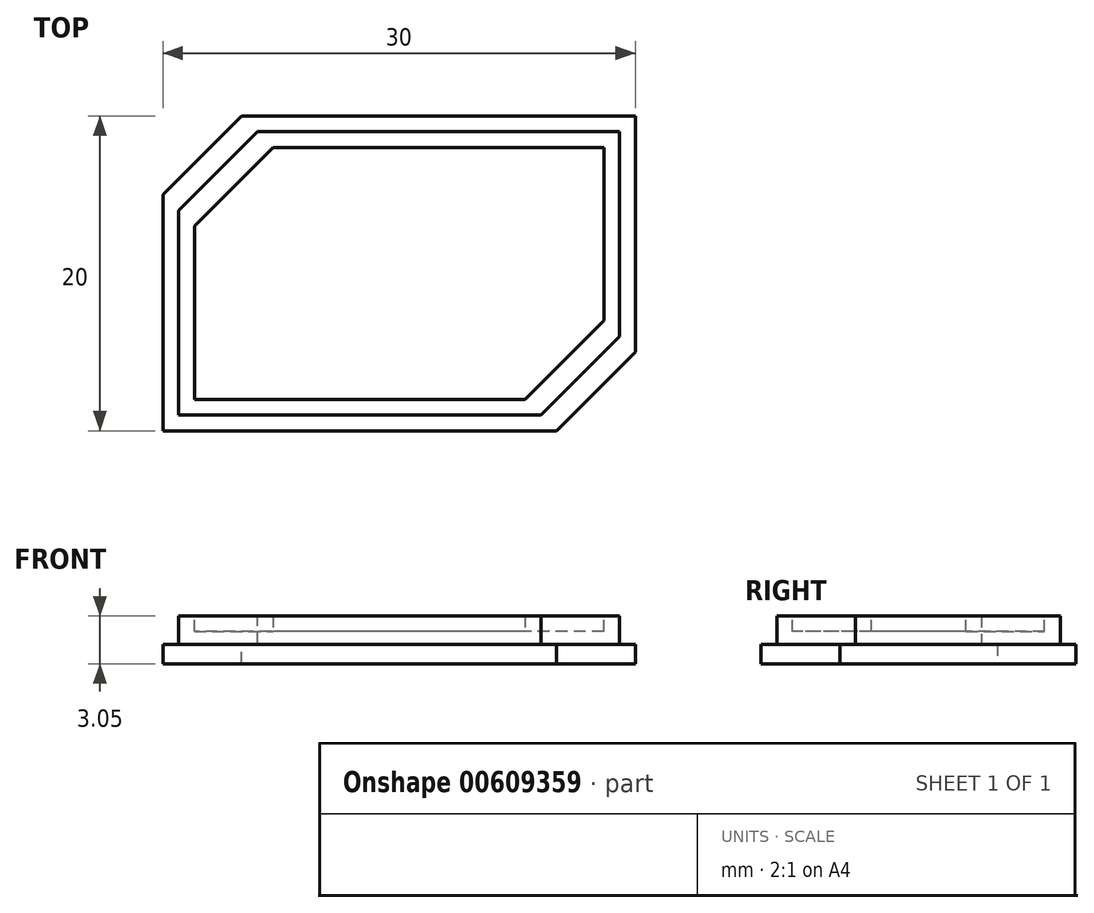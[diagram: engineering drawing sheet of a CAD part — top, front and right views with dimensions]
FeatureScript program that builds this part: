
annotation { "Feature Type Name" : "Feature", "Feature Type Description" : "" }
export const myFeature = defineFeature(function(context is Context, id is Id, definition is map)
    precondition{}
    {
        {
            var Q0;
            Q0=qCreatedBy(makeId("Top.planeOp"),FACE);
            var sketch = newSketch(context, id + "F0", { "sketchPlane" : qUnion([Q0])});
            skLineSegment(sketch, "E0.bottom", {"start": v(15, -10) * mm, "end": v(-15, -10) * mm});
            skLineSegment(sketch, "E0.top", {"start": v(15, 10) * mm, "end": v(-15, 10) * mm});
            skLineSegment(sketch, "E0.left", {"start": v(15, -10) * mm, "end": v(15, 10) * mm});
            skLineSegment(sketch, "E0.right", {"start": v(-15, -10) * mm, "end": v(-15, 10) * mm});
            skPoint(sketch, "E0.middle", {"position": v(0, 0) * mm});
            skSolve(sketch);
        }
        {
            var Q0;
            Q0=makeQuery(id+"F0.imprint","IMPRINT",FACE,{"disambiguationData":[TD([[makeQuery(id+"F0.imprint","IMPRINT",EDGE,{"derivedFrom":sQuery(id+"F0.wireOp",EDGE,"E0.bottom")}),-1.0]])]});
            extrude(context, id + "F1", {"entities" : qUnion([Q0]), "depth" : 1.25 * mm});
        }
        {
            var Q0;
            Q0=makeQuery(id+"F1.opExtrude","CAP_FACE",FACE,{"disambiguationData":[OSD([sQuery(id+"F0.wireOp",EDGE,"E0.bottom"),sQuery(id+"F0.wireOp",EDGE,"E0.top"),sQuery(id+"F0.wireOp",EDGE,"E0.left"),sQuery(id+"F0.wireOp",EDGE,"E0.right")])],"isStart":false});
            var sketch = newSketch(context, id + "F2", { "sketchPlane" : qUnion([Q0])});
            skLineSegment(sketch, "E1.bottom", {"start": v(14, -9) * mm, "end": v(-14, -9) * mm});
            skLineSegment(sketch, "E1.top", {"start": v(14, 9) * mm, "end": v(-14, 9) * mm});
            skLineSegment(sketch, "E1.left", {"start": v(14, -9) * mm, "end": v(14, 9) * mm});
            skLineSegment(sketch, "E1.right", {"start": v(-14, -9) * mm, "end": v(-14, 9) * mm});
            skPoint(sketch, "E1.middle", {"position": v(0, 0) * mm});
            skSolve(sketch);
        }
        {
            var Q0;
            Q0=makeQuery(id+"F2.imprint","IMPRINT",FACE,{"disambiguationData":[TD([[makeQuery(id+"F2.imprint","IMPRINT",EDGE,{"derivedFrom":sQuery(id+"F2.wireOp",EDGE,"E1.bottom")}),-1.0]])]});
            extrude(context, id + "F3", {"entities" : qUnion([Q0]), "operationType" : NewBodyOperationType.ADD, "depth" : 1.8 * mm, "offsetDistance" : 25 * mm});
        }
        {
            var Q0;
            Q0=makeQuery(id+"F3.opExtrude","CAP_FACE",FACE,{"disambiguationData":[OSD([sQuery(id+"F2.wireOp",EDGE,"E1.bottom"),sQuery(id+"F2.wireOp",EDGE,"E1.top"),sQuery(id+"F2.wireOp",EDGE,"E1.left"),sQuery(id+"F2.wireOp",EDGE,"E1.right")])],"isStart":false});
            var sketch = newSketch(context, id + "F4", { "sketchPlane" : qUnion([Q0])});
            skLineSegment(sketch, "E2.bottom", {"start": v(13, 8) * mm, "end": v(-13, 8) * mm});
            skLineSegment(sketch, "E2.top", {"start": v(13, -8) * mm, "end": v(-13, -8) * mm});
            skLineSegment(sketch, "E2.left", {"start": v(13, 8) * mm, "end": v(13, -8) * mm});
            skLineSegment(sketch, "E2.right", {"start": v(-13, 8) * mm, "end": v(-13, -8) * mm});
            skPoint(sketch, "E2.middle", {"position": v(0, 0) * mm});
            skSolve(sketch);
        }
        {
            var Q0;
            Q0=makeQuery(id+"F4.imprint","IMPRINT",FACE,{"disambiguationData":[TD([[makeQuery(id+"F4.imprint","IMPRINT",EDGE,{"derivedFrom":sQuery(id+"F4.wireOp",EDGE,"E2.bottom")}),1.0]])]});
            extrude(context, id + "F5", {"entities" : qUnion([Q0]), "operationType" : NewBodyOperationType.REMOVE, "oppositeDirection" : true, "depth" : 1 * mm, "offsetDistance" : 25 * mm});
        }
        {
            var Q0;
            Q0=makeQuery(id+"F5.boolean.opBoolean","COPY",EDGE,{"derivedFrom":makeQuery(id+"F5.opExtrude","SWEPT_EDGE",EDGE,{"disambiguationData":[OSD([sQuery(id+"F4.wireOp",EDGE,"E2.bottom"),sQuery(id+"F4.wireOp",EDGE,"E2.right")])]})});
            var Q1;
            Q1=makeQuery(id+"F5.boolean.opBoolean","COPY",EDGE,{"derivedFrom":makeQuery(id+"F5.opExtrude","SWEPT_EDGE",EDGE,{"disambiguationData":[OSD([sQuery(id+"F4.wireOp",EDGE,"E2.top"),sQuery(id+"F4.wireOp",EDGE,"E2.left")])]})});
            var Q2;
            Q2=makeQuery(id+"F3.opExtrude","SWEPT_EDGE",EDGE,{"disambiguationData":[OSD([sQuery(id+"F2.wireOp",EDGE,"E1.top"),sQuery(id+"F2.wireOp",EDGE,"E1.right")])]});
            var Q3;
            Q3=makeQuery(id+"F3.opExtrude","SWEPT_EDGE",EDGE,{"disambiguationData":[OSD([sQuery(id+"F2.wireOp",EDGE,"E1.bottom"),sQuery(id+"F2.wireOp",EDGE,"E1.left")])]});
            chamfer(context, id + "F6", {"entities" : qUnion([Q0, Q1, Q2, Q3]), "width" : 5 * mm, "tangentPropagation" : true});
        }
        {
            var Q0;
            Q0=makeQuery(id+"F1.opExtrude","SWEPT_EDGE",EDGE,{"disambiguationData":[OSD([sQuery(id+"F0.wireOp",EDGE,"E0.bottom"),sQuery(id+"F0.wireOp",EDGE,"E0.left")])]});
            var Q1;
            Q1=makeQuery(id+"F1.opExtrude","SWEPT_EDGE",EDGE,{"disambiguationData":[OSD([sQuery(id+"F0.wireOp",EDGE,"E0.top"),sQuery(id+"F0.wireOp",EDGE,"E0.right")])]});
            chamfer(context, id + "F7", {"entities" : qUnion([Q0, Q1]), "width" : 5 * mm, "tangentPropagation" : true});
        }
    });
